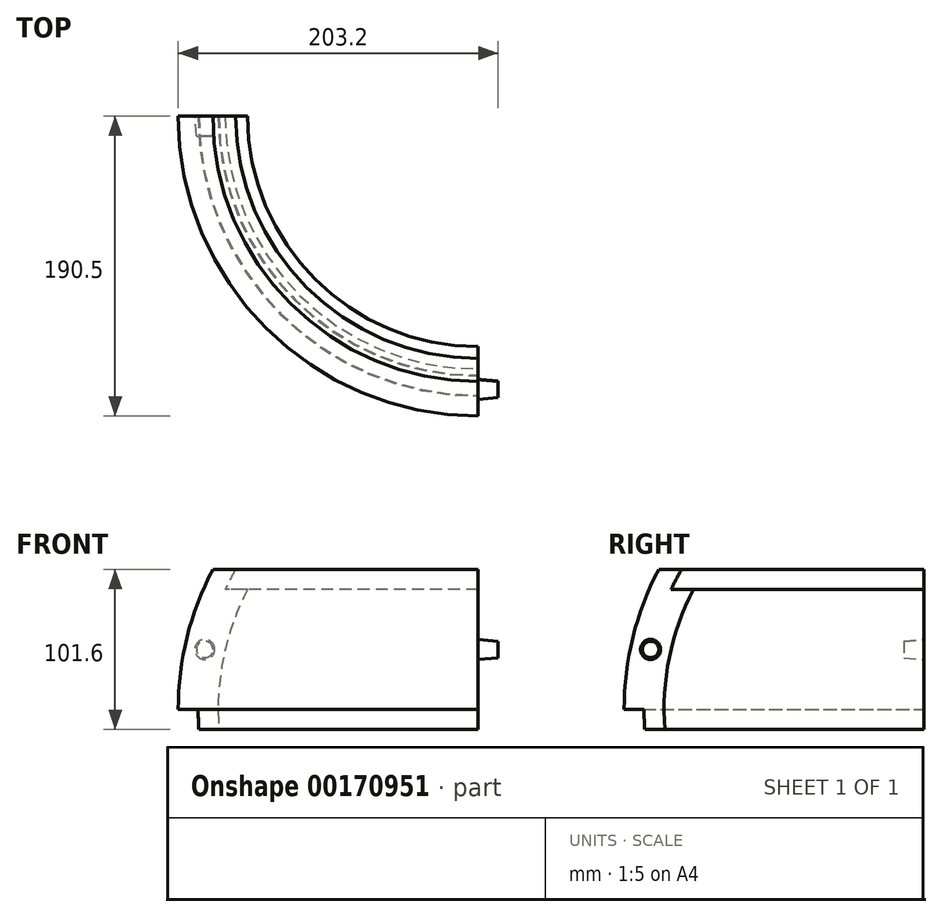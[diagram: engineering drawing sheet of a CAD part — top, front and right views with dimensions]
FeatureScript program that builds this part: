
annotation { "Feature Type Name" : "Feature", "Feature Type Description" : "" }
export const myFeature = defineFeature(function(context is Context, id is Id, definition is map)
    precondition{}
    {
        {
            var Q0;
            Q0=qCreatedBy(makeId("Front.planeOp"),FACE);
            var sketch = newSketch(context, id + "F0", { "sketchPlane" : qUnion([Q0])});
            skArc(sketch, "E0", {"start": v(-177.8, 0) * mm, "mid": v(-177.69, -6.35) * mm, "end": v(-177.35, -12.7) * mm});
            skLineSegment(sketch, "E1", {"start": v(0, 0) * mm, "end": v(-164.94, 0) * mm});
            skLineSegment(sketch, "E2", {"start": v(0, 0) * mm, "end": v(0, 76.2) * mm});
            skLineSegment(sketch, "E3", {"start": v(0, 76.2) * mm, "end": v(-160.64, 76.2) * mm});
            skLineSegment(sketch, "E4", {"start": v(-177.35, -12.7) * mm, "end": v(-164.61, -12.7) * mm});
            skArc(sketch, "E5", {"start": v(-160.64, 76.2) * mm, "mid": v(-157.44, 82.62) * mm, "end": v(-153.98, 88.9) * mm});
            skArc(sketch, "E6", {"start": v(-146.46, 76.2) * mm, "mid": v(-160.37, 39.22) * mm, "end": v(-165.1, 0) * mm});
            skLineSegment(sketch, "E7", {"start": v(-168.48, 88.9) * mm, "end": v(-153.98, 88.9) * mm});
            skLineSegment(sketch, "E8", {"start": v(-190.5, 0) * mm, "end": v(-177.8, 0) * mm});
            skArc(sketch, "E9", {"start": v(-165.1, 0) * mm, "mid": v(-164.98, -6.35) * mm, "end": v(-164.61, -12.7) * mm});
            skArc(sketch, "E10", {"start": v(-168.48, 88.9) * mm, "mid": v(-184.91, 45.8) * mm, "end": v(-190.5, 0) * mm});
            skSolve(sketch);
        }
        {
            var Q0;
            Q0=makeQuery(id+"F0.imprint","IMPRINT",FACE,{"disambiguationData":[TD([[makeQuery(id+"F0.imprint","IMPRINT",EDGE,{"derivedFrom":sQuery(id+"F0.wireOp",EDGE,"24J7LYrZ-RmTN-yFvY-N0UW-cn8gKOAgywqT")}),1.0]])]});
            var Q1;
            {var subQ1=sQuery(id+"F0.wireOp",EDGE,"E4");Q1=makeQuery(id+"F0.imprint","IMPRINT",FACE,{"disambiguationData":[TD([[makeQuery(id+"F0.imprint","IMPRINT",EDGE,{"derivedFrom":subQ1}),1.0]])]});}
            var Q2;
            Q2=sQuery(id+"F0.wireOp",EDGE,"E2");
            revolve(context, id + "F1", {"entities" : qUnion([Q0, Q1]), "axis" : qUnion([Q2]), "revolveType" : RevolveType.ONE_DIRECTION, "angle" : 90 * degree});
        }
        {
            var Q0;
            Q0=makeQuery(id+"F1.opRevolve","CAP_FACE",FACE,{"disambiguationData":[OSD([sQuery(id+"F0.wireOp",EDGE,"24J7LYrZ-RmTN-yFvY-N0UW-cn8gKOAgywqT"),sQuery(id+"F0.wireOp",EDGE,"xZ2l576y-JX5H-KU4O-jUDl-Rg5LnOSOjPA1"),sQuery(id+"F0.wireOp",EDGE,"E0"),sQuery(id+"F0.wireOp",EDGE,"E3"),sQuery(id+"F0.wireOp",EDGE,"n9Q5tiiF-cuQS-Ukv3-NaMv-KYLlYyfww3zF"),sQuery(id+"F0.wireOp",EDGE,"cXlwOLml-Ehmb-zVbi-vxee-qQtvkCD6g39N"),sQuery(id+"F0.wireOp",EDGE,"c22e73c3-7947-4e30-93bc-40cce4e0cdef"),sQuery(id+"F0.wireOp",EDGE,"953ffe04-444b-4359-8813-72619d9c4354"),sQuery(id+"F0.wireOp",EDGE,"833ff920-3a7d-46b1-9ab8-237b4e480b96")])],"isStart":false});
            var sketch = newSketch(context, id + "F2", { "sketchPlane" : qUnion([Q0])});
            skCircle(sketch, "E11", {"center": v(-173.67, 38.1) * mm, "radius": 6.35 * mm});
            skSolve(sketch);
        }
        {
            var Q0;
            Q0=makeQuery(id+"F2.imprint","IMPRINT",FACE,{"disambiguationData":[TD([[makeQuery(id+"F2.imprint","IMPRINT",EDGE,{"derivedFrom":sQuery(id+"F2.wireOp",EDGE,"E11")}),1.0]])]});
            var Q1;
            Q1=sQuery(id+"F2.wireOp",EDGE,"E11");
            extrude(context, id + "F3", {"entities" : qUnion([Q0]), "operationType" : NewBodyOperationType.ADD, "surfaceEntities" : qUnion([Q1]), "depth" : 12.7 * mm, "hasDraft" : true, "draftAngle" : 5 * degree, "draftPullDirection" : true});
        }
        {
            var Q0;
            Q0=makeQuery(id+"F1.opRevolve","CAP_FACE",FACE,{"disambiguationData":[OSD([sQuery(id+"F0.wireOp",EDGE,"24J7LYrZ-RmTN-yFvY-N0UW-cn8gKOAgywqT"),sQuery(id+"F0.wireOp",EDGE,"E0"),sQuery(id+"F0.wireOp",EDGE,"E3"),sQuery(id+"F0.wireOp",EDGE,"833ff920-3a7d-46b1-9ab8-237b4e480b96"),sQuery(id+"F0.wireOp",EDGE,"E4"),sQuery(id+"F0.wireOp",EDGE,"E5"),sQuery(id+"F0.wireOp",EDGE,"E6"),sQuery(id+"F0.wireOp",EDGE,"E7"),sQuery(id+"F0.wireOp",EDGE,"E8"),sQuery(id+"F0.wireOp",EDGE,"E9")])],"isStart":true});
            var sketch = newSketch(context, id + "F4", { "sketchPlane" : qUnion([Q0])});
            skCircle(sketch, "E12", {"center": v(173.67, 38.1) * mm, "radius": 6.35 * mm});
            skSolve(sketch);
        }
        {
            var Q0;
            Q0=makeQuery(id+"F4.imprint","IMPRINT",FACE,{"disambiguationData":[TD([[makeQuery(id+"F4.imprint","IMPRINT",EDGE,{"derivedFrom":sQuery(id+"F4.wireOp",EDGE,"E12")}),1.0]])]});
            var Q1;
            Q1=sQuery(id+"F4.wireOp",EDGE,"E12");
            extrude(context, id + "F5", {"entities" : qUnion([Q0]), "operationType" : NewBodyOperationType.REMOVE, "surfaceEntities" : qUnion([Q1]), "oppositeDirection" : true, "depth" : 12.7 * mm, "hasDraft" : true, "draftAngle" : 5 * degree, "draftPullDirection" : true});
        }
    });
